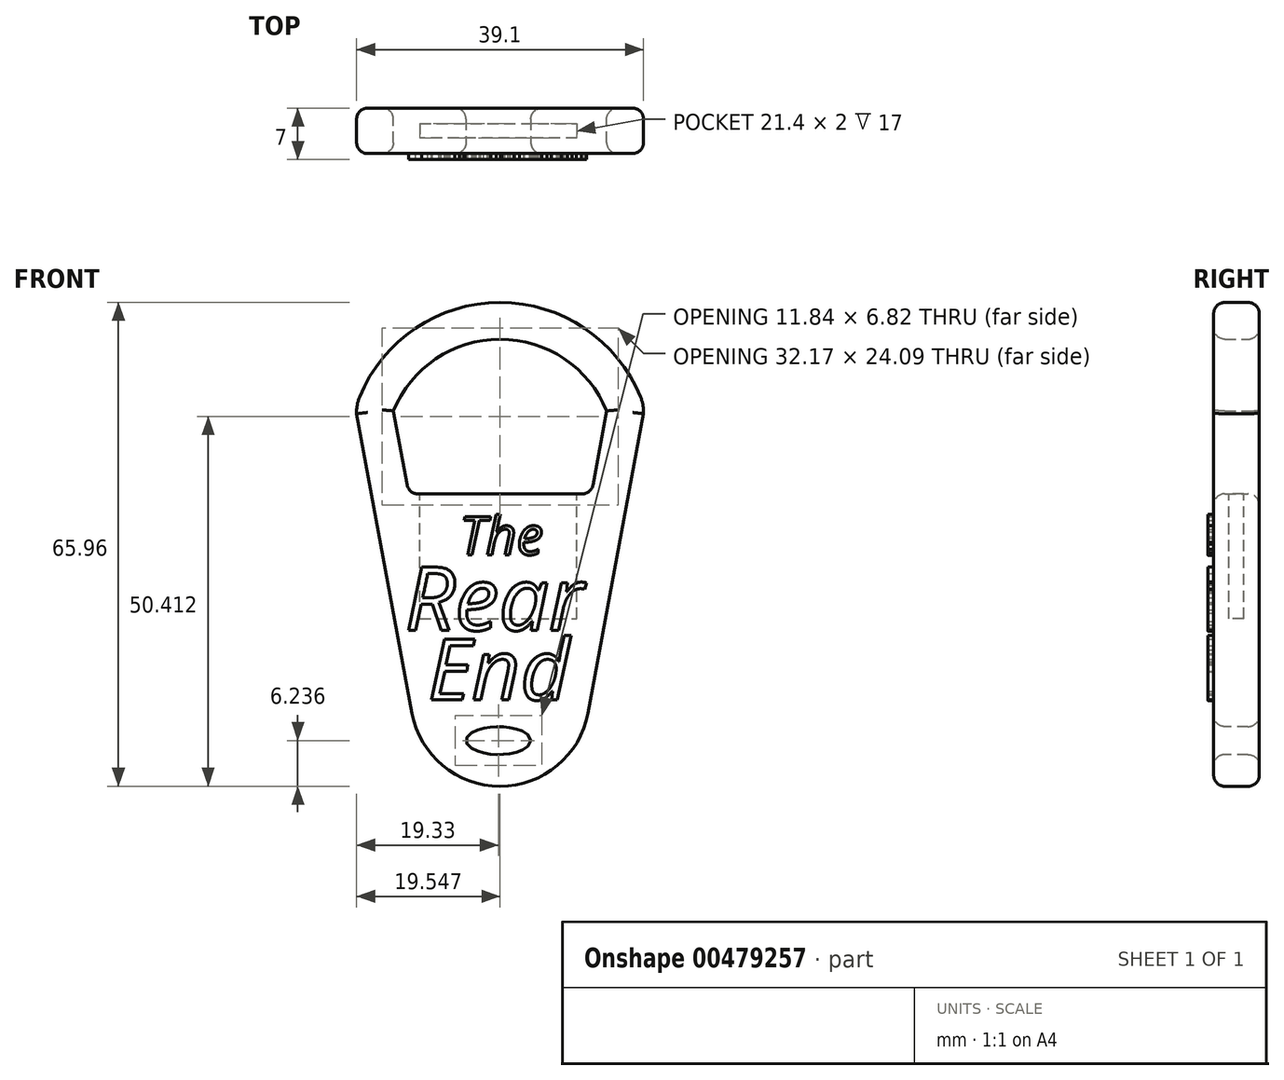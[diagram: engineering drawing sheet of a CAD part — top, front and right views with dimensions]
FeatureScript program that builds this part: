
annotation { "Feature Type Name" : "Feature", "Feature Type Description" : "" }
export const myFeature = defineFeature(function(context is Context, id is Id, definition is map)
    precondition{}
    {
        {
            var Q0;
            Q0=qCreatedBy(makeId("Front.planeOp"),FACE);
            var sketch = newSketch(context, id + "F0", { "sketchPlane" : qUnion([Q0])});
            skLineSegment(sketch, "E0", {"start": v(0.22, 53.5) * mm, "end": v(0.22, -27.22) * mm, "construction": true});
            skLineSegment(sketch, "E1", {"start": v(19.76, 12.33) * mm, "end": v(12.22, -28.48) * mm});
            skLineSegment(sketch, "E2.MirrorCS", {"start": v(-19.33, 12.33) * mm, "end": v(-11.78, -28.48) * mm});
            skLineSegment(sketch, "E3.0", {"start": v(-14.31, 12.71) * mm, "end": v(-12.22, 1.4) * mm});
            skLineSegment(sketch, "E3.3", {"start": v(14.75, 12.71) * mm, "end": v(12.66, 1.4) * mm});
            skLineSegment(sketch, "E4", {"start": v(-12.22, 1.4) * mm, "end": v(12.66, 1.4) * mm});
            skPoint(sketch, "E5", {"position": v(0.22, 20.6) * mm});
            skPoint(sketch, "E6", {"position": v(-14.31, 12.71) * mm});
            skPoint(sketch, "E7.MirrorP", {"position": v(14.75, 12.71) * mm});
            skArc(sketch, "E8", {"start": v(14.75, 12.71) * mm, "mid": v(0.22, 22.5) * mm, "end": v(-14.31, 12.71) * mm});
            skArc(sketch, "E9.0", {"start": v(19.62, 13.97) * mm, "mid": v(0.56, 27.5) * mm, "end": v(-18.94, 14.6) * mm});
            skArc(sketch, "E10", {"start": v(-18.94, 14.6) * mm, "mid": v(-19.26, 13.5) * mm, "end": v(-19.33, 12.33) * mm});
            skArc(sketch, "E11.MirrorCS", {"start": v(19.38, 14.6) * mm, "mid": v(19.7, 13.5) * mm, "end": v(19.76, 12.33) * mm});
            skPoint(sketch, "E12.orphan", {"position": v(-21.9, 26.19) * mm});
            skPoint(sketch, "E13.orphan", {"position": v(22.32, 26.19) * mm});
            skPoint(sketch, "E14.MirrorCS.start.orphan", {"position": v(0.22, 25.6) * mm});
            skArc(sketch, "E15", {"start": v(-11.78, -28.48) * mm, "mid": v(0.22, -38.46) * mm, "end": v(12.22, -28.48) * mm});
            skPoint(sketch, "E16.MirrorCS.end.orphan", {"position": v(0.22, -28.48) * mm});
            skPoint(sketch, "E16.MirrorCS.start.orphan", {"position": v(-11.78, -28.48) * mm});
            skLineSegment(sketch, "E17", {"start": v(-11.78, -28.48) * mm, "end": v(12.22, -28.48) * mm, "construction": true});
            skSolve(sketch);
        }
        {
            var Q0;
            Q0=qSketchRegion(id+"F0",true);
            extrude(context, id + "F1", {"entities" : qUnion([Q0]), "depth" : 6.2 * mm});
        }
        {
            var Q0;
            Q0=makeQuery(id+"F1.opExtrude","CAP_FACE",FACE,{"disambiguationData":[OSD([sQuery(id+"F0.wireOp",EDGE,"E1"),sQuery(id+"F0.wireOp",EDGE,"E2.MirrorCS"),sQuery(id+"F0.wireOp",EDGE,"E3.0"),sQuery(id+"F0.wireOp",EDGE,"E3.3"),sQuery(id+"F0.wireOp",EDGE,"E4"),sQuery(id+"F0.wireOp",EDGE,"E8"),sQuery(id+"F0.wireOp",EDGE,"E9.0"),sQuery(id+"F0.wireOp",EDGE,"E10"),sQuery(id+"F0.wireOp",EDGE,"E11.MirrorCS"),sQuery(id+"F0.wireOp",EDGE,"E15")])],"isStart":false});
            var sketch = newSketch(context, id + "F2", { "sketchPlane" : qUnion([Q0])});
            skEllipse(sketch, "E18", {"center": v(0, -32.22) * mm, "majorRadius": 4.42 * mm, "minorRadius": 1.9 * mm, "majorAxis": v(1, 0)});
            skSolve(sketch);
        }
        {
            var Q0;
            Q0=makeQuery(id+"F2.imprint","IMPRINT",FACE,{"disambiguationData":[TD([[makeQuery(id+"F2.imprint","IMPRINT",EDGE,{"derivedFrom":sQuery(id+"F2.wireOp",EDGE,"E18")}),1.0]])]});
            extrude(context, id + "F3", {"entities" : qUnion([Q0]), "operationType" : NewBodyOperationType.REMOVE, "oppositeDirection" : true, "depth" : 6.5 * mm});
        }
        {
            var Q0;
            Q0=makeQuery(id+"F1.opExtrude","SWEPT_FACE",FACE,{"disambiguationData":[OSD([sQuery(id+"F0.wireOp",EDGE,"E4")])]});
            var sketch = newSketch(context, id + "F4", { "sketchPlane" : qUnion([Q0])});
            skLineSegment(sketch, "E19", {"start": v(0, -2.1) * mm, "end": v(10.7, -2.1) * mm});
            skLineSegment(sketch, "E20.0", {"start": v(0, -4.1) * mm, "end": v(10.7, -4.1) * mm});
            skLineSegment(sketch, "E21", {"start": v(10.7, -2.1) * mm, "end": v(10.7, -4.1) * mm});
            skLineSegment(sketch, "E22", {"start": v(0, -2.1) * mm, "end": v(0, -4.1) * mm, "construction": true});
            skLineSegment(sketch, "E23.MirrorCS", {"start": v(0, -2.1) * mm, "end": v(-10.7, -2.1) * mm});
            skLineSegment(sketch, "E24.MirrorCS", {"start": v(-10.7, -2.1) * mm, "end": v(-10.7, -4.1) * mm});
            skLineSegment(sketch, "E25.MirrorCS", {"start": v(0, -4.1) * mm, "end": v(-10.7, -4.1) * mm});
            skSolve(sketch);
        }
        {
            var Q0;
            Q0=makeQuery(id+"F4.imprint","IMPRINT",FACE,{"disambiguationData":[TD([[makeQuery(id+"F4.imprint","IMPRINT",EDGE,{"derivedFrom":sQuery(id+"F4.wireOp",EDGE,"E19")}),-1.0]])]});
            extrude(context, id + "F5", {"entities" : qUnion([Q0]), "operationType" : NewBodyOperationType.REMOVE, "oppositeDirection" : true, "depth" : 17 * mm});
        }
        {
            var Q0;
            Q0=makeQuery(id+"F1.opExtrude","SWEPT_EDGE",EDGE,{"disambiguationData":[OSD([sQuery(id+"F0.wireOp",EDGE,"E3.0"),sQuery(id+"F0.wireOp",EDGE,"E4")])]});
            var Q1;
            Q1=makeQuery(id+"F1.opExtrude","SWEPT_EDGE",EDGE,{"disambiguationData":[OSD([sQuery(id+"F0.wireOp",EDGE,"E3.3"),sQuery(id+"F0.wireOp",EDGE,"E4")])]});
            var Q2;
            Q2=makeQuery(id+"F1.opExtrude","CAP_FACE",FACE,{"disambiguationData":[OSD([sQuery(id+"F0.wireOp",EDGE,"E1"),sQuery(id+"F0.wireOp",EDGE,"E2.MirrorCS"),sQuery(id+"F0.wireOp",EDGE,"E3.0"),sQuery(id+"F0.wireOp",EDGE,"E3.3"),sQuery(id+"F0.wireOp",EDGE,"E4"),sQuery(id+"F0.wireOp",EDGE,"E8"),sQuery(id+"F0.wireOp",EDGE,"E9.0"),sQuery(id+"F0.wireOp",EDGE,"E10"),sQuery(id+"F0.wireOp",EDGE,"E11.MirrorCS"),sQuery(id+"F0.wireOp",EDGE,"E15")])],"isStart":false});
            var Q3;
            Q3=makeQuery(id+"F1.opExtrude","CAP_FACE",FACE,{"disambiguationData":[OSD([sQuery(id+"F0.wireOp",EDGE,"E1"),sQuery(id+"F0.wireOp",EDGE,"E2.MirrorCS"),sQuery(id+"F0.wireOp",EDGE,"E3.0"),sQuery(id+"F0.wireOp",EDGE,"E3.3"),sQuery(id+"F0.wireOp",EDGE,"E4"),sQuery(id+"F0.wireOp",EDGE,"E8"),sQuery(id+"F0.wireOp",EDGE,"E9.0"),sQuery(id+"F0.wireOp",EDGE,"E10"),sQuery(id+"F0.wireOp",EDGE,"E11.MirrorCS"),sQuery(id+"F0.wireOp",EDGE,"E15")])],"isStart":true});
            fillet(context, id + "F6", {"entities" : qUnion([Q0, Q1, Q2, Q3]), "radius" : 1.5 * mm, "tangentPropagation" : true, "allowEdgeOverflow" : false});
        }
        {
            var Q0;
            Q0=makeQuery(id+"F1.opExtrude","CAP_FACE",FACE,{"disambiguationData":[OSD([sQuery(id+"F0.wireOp",EDGE,"E1"),sQuery(id+"F0.wireOp",EDGE,"E2.MirrorCS"),sQuery(id+"F0.wireOp",EDGE,"E3.0"),sQuery(id+"F0.wireOp",EDGE,"E3.3"),sQuery(id+"F0.wireOp",EDGE,"E4"),sQuery(id+"F0.wireOp",EDGE,"E8"),sQuery(id+"F0.wireOp",EDGE,"E9.0"),sQuery(id+"F0.wireOp",EDGE,"E10"),sQuery(id+"F0.wireOp",EDGE,"E11.MirrorCS"),sQuery(id+"F0.wireOp",EDGE,"E15")])],"isStart":false});
            var sketch = newSketch(context, id + "F7", { "sketchPlane" : qUnion([Q0])});
            skText(sketch, "E26", { "text": "Rear", "fontName": "OpenSans-Italic.ttf"});
            skText(sketch, "E27", { "text": "End", "fontName": "OpenSans-Italic.ttf"});
            skText(sketch, "E28", { "text": "The", "fontName": "OpenSans-Italic.ttf"});
            const initialGuessF7  = {"E26": [-0.01278, -0.0172, 1, 0, 0.00869], "E27": [-0.0096, -0.02667, 1, 0, 0.00834], "E28": [-0.00533, -0.00689, 1, 0, 0.00524]};
            skSetInitialGuess(sketch, initialGuessF7);
            skSolve(sketch);
        }
        {
            var Q0;
            Q0 = qSketchRegion(id + "F7", true);
            extrude(context, id + "F8", {"entities" : qUnion([Q0]), "operationType" : NewBodyOperationType.ADD, "depth" : .8 * mm, "offsetDistance" : 25 * mm});
        }
    });
